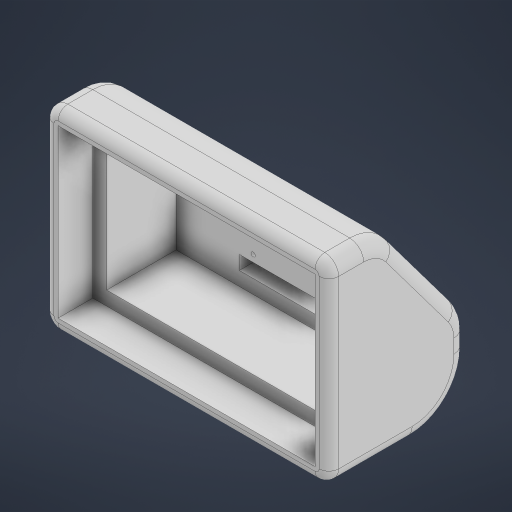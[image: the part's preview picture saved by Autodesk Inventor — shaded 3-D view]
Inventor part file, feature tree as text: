
AUTODESK INVENTOR PART (.ipt)
format: ipt  version: 2023 (Build 270158000, 158)  size: 320,512 bytes
history: native  units: mm
features: extrude x7, fillet x5, sketch x4, chamfer x2
ambient origin geometry x8: Origin, YZ Plane, XZ Plane, XY Plane, X Axis, Y Axis, Z Axis, Center Point
bodies: Solid1 (feature_tree)
feature tree (18):
  sketch  "Sketch1"  dims[d0=185.0mm d1=120.0mm]
  extrude  "Extrusion1"  Depth=120.0mm
  extrude  "Extrusion2"  Depth=10.0mm
  fillet  "Fillet1"  Radius=205.0mm
  chamfer  "Chamfer1"  Distance=100.0mm
  fillet  "Fillet2"  Radius=25.0mm
  fillet  "Fillet3"  Radius=7.0mm
  fillet  "Fillet4"  Radius=30.0mm
  extrude  "Extrusion3"  Depth=40.0mm
  extrude  "Extrusion4"  Depth=10.0mm
  extrude  "Extrusion5"  Depth=3.0mm
  extrude  "Extrusion6"  Depth=3.0mm
  extrude  "Extrusion7"  Depth=25.0mm TaperAngle=0.0deg
  chamfer  "Chamfer2"  Distance=10.0mm
  fillet  "Fillet5"  Radius=25.0mm
  sketch  "Sketch2"  dims[d2=10.0mm d3=10.0mm d4=205.0mm]
  sketch  "Sketch4"  dims[d5=140.0mm d6=100.0mm d7=0.0mm d8=25.0mm d9=0.0mm d10=7.0mm]
  sketch  "Sketch5"  dims[d11=80.0mm d12=60.0mm d13=45.0deg d14=30.0mm d15=40.0mm d16=10.0mm d20=3.0mm d21=3.0mm d22=25.0mm d23=0.0mm d24=10.0mm d25=25.0mm d26=0.0mm d27=25.0mm d28=0.0mm d29=10.0mm d30=25.0mm d31=0.0mm d32=25.0mm d33=0.0mm d34=25.0mm d35=60.0mm d36=45.0deg d37=30.0mm d38=26.994mm d39=53.988mm d40=10.0mm d41=10.0mm]
